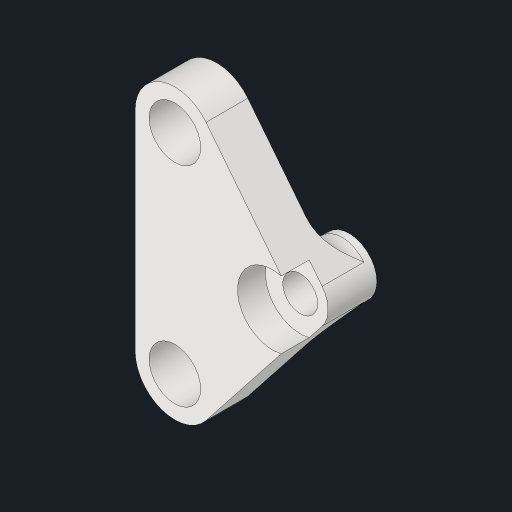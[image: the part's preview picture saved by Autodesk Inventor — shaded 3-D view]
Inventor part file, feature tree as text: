
AUTODESK INVENTOR PART (.ipt)
format: ipt  version: 2023.2 (Build 272271030, 271C)  size: 156,160 bytes
history: native  units: mm
features: extrude x3, sketch x3, fillet x1, projected_geometry x1
ambient origin geometry x8: Origin, YZ Plane, XZ Plane, XY Plane, X Axis, Y Axis, Z Axis, Center Point
bodies: Solid1 (feature_tree)
feature tree (8):
  extrude  "Extrusion1"  Depth=4.0mm
  extrude  "Extrusion3"  Depth=5.5mm
  fillet  "Fillet2"  Radius=7.0mm
  extrude  "Extrusion4"  Depth=2.0mm
  sketch  "Sketch1"  dims[d0=2.5mm d1=4.0mm]
  sketch  "Sketch3"  dims[d2=5.5mm d3=0.0mm d9=3.7mm d10=7.0mm]
  projected_geometry  "Projected Loop1"
  sketch  "Sketch4"  dims[d11=15.0mm d12=7.5mm d13=5.7mm d14=3.0mm d15=0.0mm d16=2.0mm d17=5.0mm d18=2.0mm d19=0.0mm]
